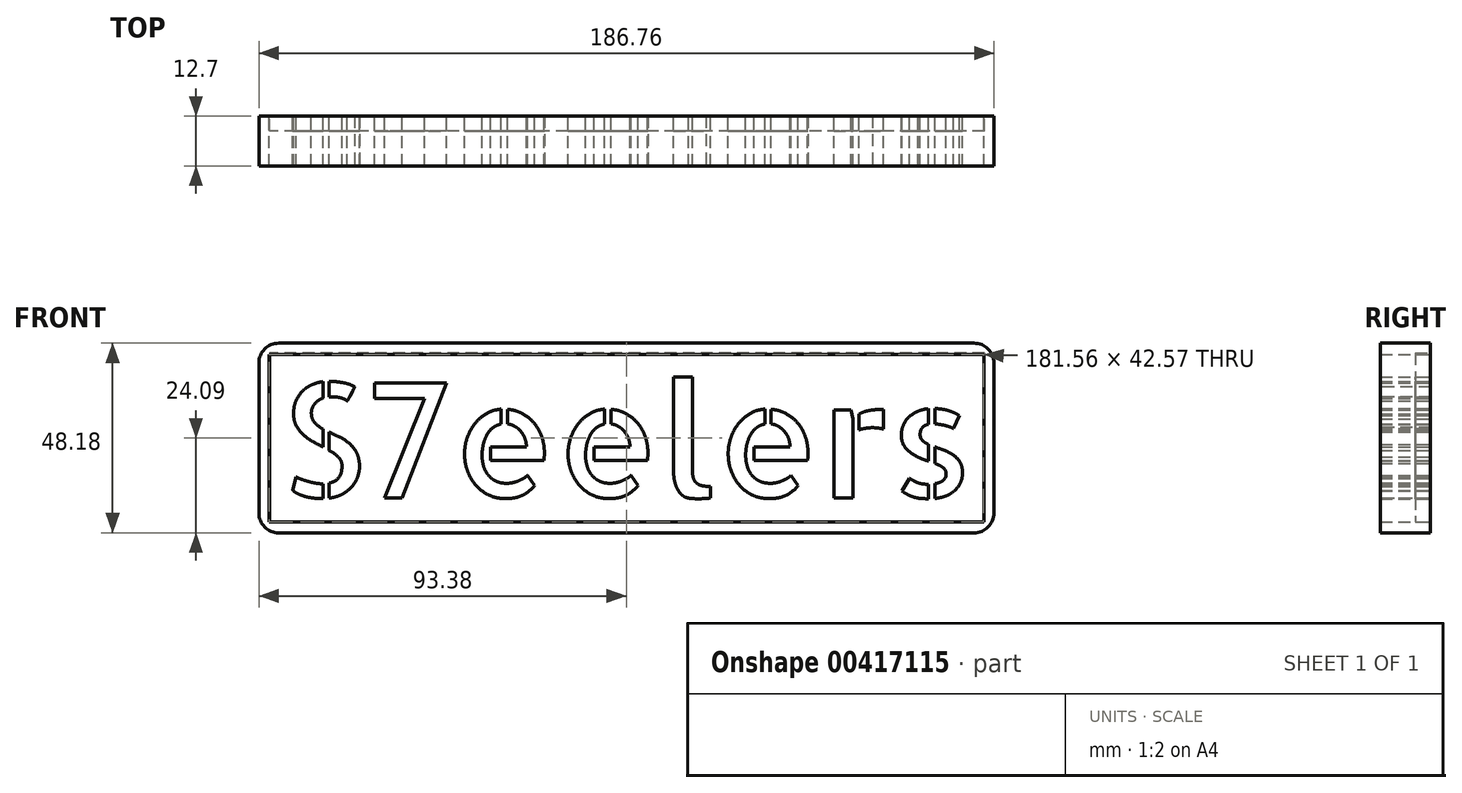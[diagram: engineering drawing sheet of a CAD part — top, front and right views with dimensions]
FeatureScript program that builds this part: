
annotation { "Feature Type Name" : "Feature", "Feature Type Description" : "" }
export const myFeature = defineFeature(function(context is Context, id is Id, definition is map)
    precondition{}
    {
        {
            var Q0;
            Q0=qCreatedBy(makeId("Front.planeOp"),FACE);
            var sketch = newSketch(context, id + "F0", { "sketchPlane" : qUnion([Q0])});
            skLineSegment(sketch, "E0.bottom", {"start": v(-93.38, 24.1) * mm, "end": v(93.38, 24.1) * mm});
            skLineSegment(sketch, "E0.top", {"start": v(-93.38, -24.1) * mm, "end": v(93.38, -24.1) * mm});
            skLineSegment(sketch, "E0.left", {"start": v(-93.38, 24.1) * mm, "end": v(-93.38, -24.1) * mm});
            skLineSegment(sketch, "E0.right", {"start": v(93.38, 24.1) * mm, "end": v(93.38, -24.1) * mm});
            skPoint(sketch, "E0.middle", {"position": v(0, 0) * mm});
            skLineSegment(sketch, "E1.bottom", {"start": v(-90.78, 21.28) * mm, "end": v(90.78, 21.28) * mm});
            skLineSegment(sketch, "E1.top", {"start": v(-90.78, -21.28) * mm, "end": v(90.78, -21.28) * mm});
            skLineSegment(sketch, "E1.left", {"start": v(-90.78, 21.28) * mm, "end": v(-90.78, -21.28) * mm});
            skLineSegment(sketch, "E1.right", {"start": v(90.78, 21.28) * mm, "end": v(90.78, -21.28) * mm});
            skSolve(sketch);
        }
        {
            var Q0;
            Q0=qCreatedBy(makeId("Front.planeOp"),FACE);
            var sketch = newSketch(context, id + "F1", { "sketchPlane" : qUnion([Q0])});
            skText(sketch, "E2", { "text": "S7eelers", "fontName": "AllertaStencil-Regular.ttf"});
            const initialGuessF1  = {"E2": [-0.08797, -0.01524, 1, 0, 0.0292]};
            skSetInitialGuess(sketch, initialGuessF1);
            skSolve(sketch);
        }
        {
            var Q0;
            Q0=makeQuery(id+"F0.imprint","IMPRINT",FACE,{"disambiguationData":[TD([[makeQuery(id+"F0.imprint","IMPRINT",EDGE,{"derivedFrom":sQuery(id+"F0.wireOp",EDGE,"E0.bottom")}),-1.0]])]});
            extrude(context, id + "F2", {"entities" : qUnion([Q0]), "depth" : 12.7 * mm});
        }
        {
            var Q0;
            Q0 = qSketchRegion(id + "F1", true);
            extrude(context, id + "F3", {"entities" : qUnion([Q0]), "depth" : 12.7 * mm});
        }
        {
            var Q0;
            Q0=qCreatedBy(makeId("Front.planeOp"),FACE);
            var sketch = newSketch(context, id + "F4", { "sketchPlane" : qUnion([Q0])});
            skLineSegment(sketch, "E3.bottom", {"start": v(90.94, 21.55) * mm, "end": v(-90.64, 21.55) * mm});
            skLineSegment(sketch, "E3.top", {"start": v(90.94, -21.32) * mm, "end": v(-90.64, -21.32) * mm});
            skLineSegment(sketch, "E3.left", {"start": v(90.94, 21.55) * mm, "end": v(90.94, -21.32) * mm});
            skLineSegment(sketch, "E3.right", {"start": v(-90.64, 21.55) * mm, "end": v(-90.64, -21.32) * mm});
            skSolve(sketch);
        }
        {
            var Q0;
            Q0 = qSketchRegion(id + "F4", true);
            var Q1;
            Q1 = qSketchRegion(id + "F1", true);
            extrude(context, id + "F5", {"entities" : qUnion([Q0, Q1]), "depth" : 3.8 * mm});
        }
        {
            var Q0;
            Q0=makeQuery(id+"F2.opExtrude","SWEPT_EDGE",EDGE,{"disambiguationData":[OSD([sQuery(id+"F0.wireOp",EDGE,"E0.bottom"),sQuery(id+"F0.wireOp",EDGE,"E0.left")])]});
            var Q1;
            Q1=makeQuery(id+"F2.opExtrude","SWEPT_EDGE",EDGE,{"disambiguationData":[OSD([sQuery(id+"F0.wireOp",EDGE,"E0.top"),sQuery(id+"F0.wireOp",EDGE,"E0.left")])]});
            var Q2;
            Q2=makeQuery(id+"F2.opExtrude","SWEPT_EDGE",EDGE,{"disambiguationData":[OSD([sQuery(id+"F0.wireOp",EDGE,"E0.top"),sQuery(id+"F0.wireOp",EDGE,"E0.right")])]});
            var Q3;
            Q3=makeQuery(id+"F2.opExtrude","SWEPT_EDGE",EDGE,{"disambiguationData":[OSD([sQuery(id+"F0.wireOp",EDGE,"E0.bottom"),sQuery(id+"F0.wireOp",EDGE,"E0.right")])]});
            fillet(context, id + "F6", {"entities" : qUnion([Q0, Q1, Q2, Q3]), "radius" : 5.08 * mm, "tangentPropagation" : true, "allowEdgeOverflow" : false});
        }
    });
